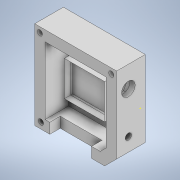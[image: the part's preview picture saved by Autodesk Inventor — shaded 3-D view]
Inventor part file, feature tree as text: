
AUTODESK INVENTOR PART (.ipt)
format: ipt  version: 2020 (Build 240168000, 168)  size: 254,464 bytes
history: native  units: mm
features: extrude x8, sketch x7, shell x1, fillet x1
ambient origin geometry x8: Origin, YZ Plane, XZ Plane, XY Plane, X Axis, Y Axis, Z Axis, Center Point
bodies: Solid1 (feature_tree)
feature tree (17):
  extrude  "Extrusion1"  Depth=32.25mm
  shell  "Shell2"  Thickness=11.25mm
  extrude  "Extrusion3"  Depth=2.5mm
  extrude  "Extrusion11"  TaperAngle=0.0deg  [1 undecoded]
  extrude  "Extrusion13"  Depth=5.0mm
  extrude  "Extrusion14"  Depth=2.5mm
  extrude  "Extrusion15"  Depth=20.0mm
  sketch  "Sketch16"  dims[d57=2.8mm d58=2.5mm]
  extrude  "Extrusion16"  Depth=1.0mm
  fillet  "Fillet1"  Radius=1.0mm
  extrude  "Extrusion17"  Depth=17.25mm
  sketch  "Sketch11"  dims[d0=29.25mm d1=32.25mm d4=11.25mm d5=0.0mm]
  sketch  "Sketch13"  dims[d13=5.0mm d14=2.5mm]
  sketch  "Sketch14"  dims[d15=2.5mm d17=0.0mm d18=0.0mm]
  sketch  "Sketch15"  dims[d51=5.0mm d52=0.0mm d56=2.8mm]
  sketch  "Sketch17"  dims[d60=20.0mm d61=6.5mm]
  sketch  "Sketch18"  dims[d64=10.0mm d65=0.0mm d66=1.0mm d67=1.0mm d69=17.25mm d70=14.75mm d71=1.0mm d72=5.0mm d73=3.0mm d74=0.0mm d75=2.5mm d76=0.0mm d77=3.0mm d79=2.5mm d80=0.0mm d81=10.25mm d82=6.5mm d83=1.0mm d84=1.0mm d85=2.5mm d86=5.625mm d87=7.25mm d88=9.1mm d92=2.5mm d93=0.0mm d89=0.5mm d90=0.872665mm d91=0.5mm]
note: 1 required parameter value undecoded (feature->parameter linkage not recoverable at this tier; creation-order binding heuristic only, values carry confidence <= 0.55)
